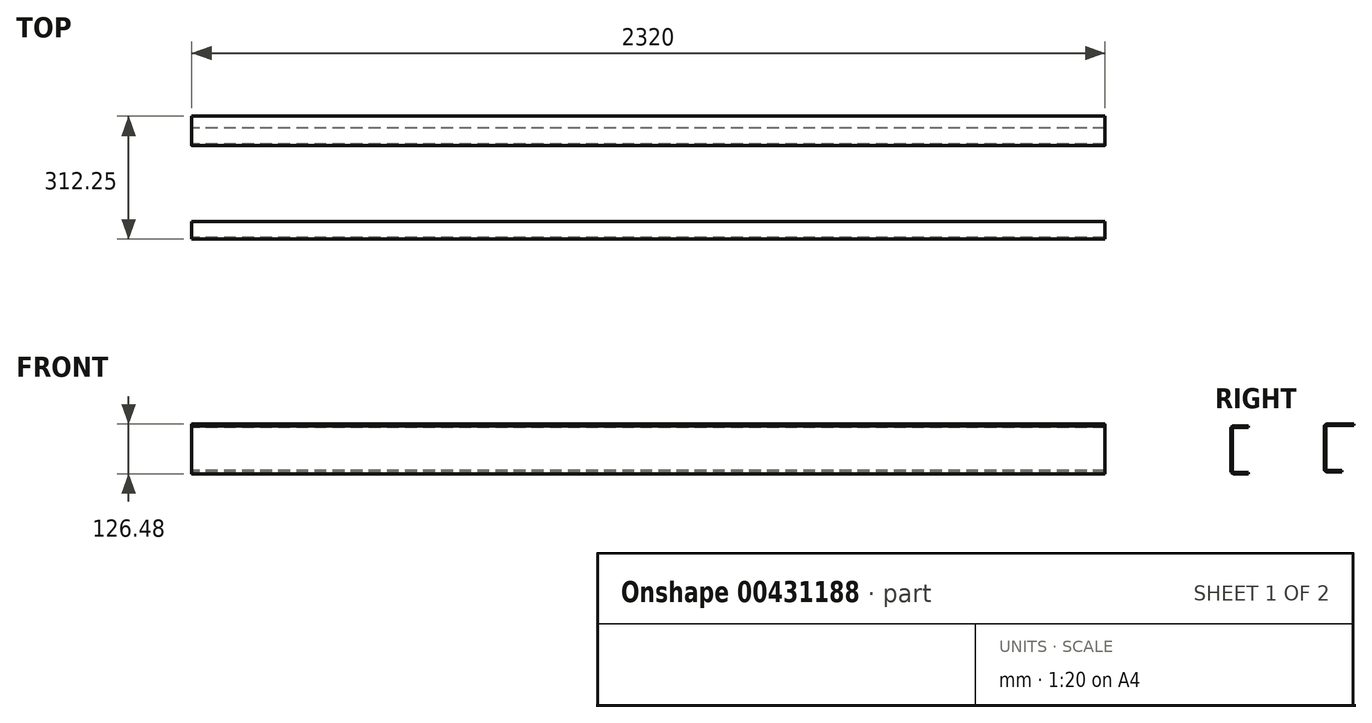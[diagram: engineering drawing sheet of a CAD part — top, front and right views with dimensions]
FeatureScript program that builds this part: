
annotation { "Feature Type Name" : "Feature", "Feature Type Description" : "" }
export const myFeature = defineFeature(function(context is Context, id is Id, definition is map)
    precondition{}
    {
        {
            var Q0;
            Q0=qCreatedBy(makeId("Right.planeOp"),FACE);
            var sketch = newSketch(context, id + "F0", { "sketchPlane" : qUnion([Q0])});
            skLineSegment(sketch, "E0", {"start": v(0, 8) * mm, "end": v(0, 114) * mm});
            skLineSegment(sketch, "E1", {"start": v(8, 122) * mm, "end": v(45, 122) * mm});
            skLineSegment(sketch, "E2", {"start": v(8, 0) * mm, "end": v(45, 0) * mm});
            skLineSegment(sketch, "E3.0", {"start": v(8, 118) * mm, "end": v(45, 118) * mm});
            skLineSegment(sketch, "E4.0", {"start": v(4, 8) * mm, "end": v(4, 114) * mm});
            skLineSegment(sketch, "E5.0", {"start": v(8, 4) * mm, "end": v(45, 4) * mm});
            skLineSegment(sketch, "E6", {"start": v(45, 118) * mm, "end": v(45, 122) * mm});
            skLineSegment(sketch, "E7", {"start": v(45, 0) * mm, "end": v(45, 4) * mm});
            skPoint(sketch, "E8.visualSharp", {"position": v(0, 122) * mm});
            skPoint(sketch, "E9.visualSharp", {"position": v(4, 118) * mm});
            skArc(sketch, "E9.filletArc", {"start": v(8, 118) * mm, "mid": v(5.17, 116.83) * mm, "end": v(4, 114) * mm});
            skArc(sketch, "E10.0", {"start": v(8, 122) * mm, "mid": v(2.34, 119.66) * mm, "end": v(0, 114) * mm});
            skPoint(sketch, "E11.visualSharp", {"position": v(4, 4) * mm});
            skArc(sketch, "E11.filletArc", {"start": v(4, 8) * mm, "mid": v(5.17, 5.17) * mm, "end": v(8, 4) * mm});
            skArc(sketch, "E12.0", {"start": v(0, 8) * mm, "mid": v(2.34, 2.34) * mm, "end": v(8, 0) * mm});
            skPoint(sketch, "E13.orphan", {"position": v(0, 0) * mm});
            skSolve(sketch);
        }
        {
            var Q0;
            Q0=makeQuery(id+"F0.imprint","IMPRINT",FACE,{"disambiguationData":[TD([[makeQuery(id+"F0.imprint","IMPRINT",EDGE,{"derivedFrom":sQuery(id+"F0.wireOp",EDGE,"E0")}),-1.0]])]});
            extrude(context, id + "F1", {"entities" : qUnion([Q0]), "depth" : 2320 * mm});
        }
        {
            var Q0;
            Q0=qCreatedBy(makeId("Right.planeOp"),FACE);
            var sketch = newSketch(context, id + "F2", { "sketchPlane" : qUnion([Q0])});
            skLineSegment(sketch, "E14", {"start": v(237.25, 12.48) * mm, "end": v(237.25, 118.48) * mm});
            skLineSegment(sketch, "E15", {"start": v(245.25, 126.48) * mm, "end": v(312.25, 126.48) * mm});
            skLineSegment(sketch, "E16", {"start": v(245.25, 4.48) * mm, "end": v(282.25, 4.48) * mm});
            skLineSegment(sketch, "E17.0", {"start": v(245.25, 122.48) * mm, "end": v(312.25, 122.48) * mm});
            skLineSegment(sketch, "E18.0", {"start": v(241.25, 12.48) * mm, "end": v(241.25, 118.48) * mm});
            skLineSegment(sketch, "E19.0", {"start": v(245.25, 8.48) * mm, "end": v(282.25, 8.48) * mm});
            skLineSegment(sketch, "E20", {"start": v(312.25, 122.48) * mm, "end": v(312.25, 126.48) * mm});
            skLineSegment(sketch, "E21", {"start": v(282.25, 4.48) * mm, "end": v(282.25, 8.48) * mm});
            skPoint(sketch, "E22.visualSharp", {"position": v(237.25, 126.48) * mm});
            skPoint(sketch, "E23.visualSharp", {"position": v(241.25, 122.48) * mm});
            skArc(sketch, "E23.filletArc", {"start": v(245.25, 122.48) * mm, "mid": v(242.42, 121.3) * mm, "end": v(241.25, 118.48) * mm});
            skArc(sketch, "E24.0", {"start": v(245.25, 126.48) * mm, "mid": v(239.6, 124.14) * mm, "end": v(237.25, 118.48) * mm});
            skPoint(sketch, "E25.visualSharp", {"position": v(241.25, 8.48) * mm});
            skArc(sketch, "E25.filletArc", {"start": v(241.25, 12.48) * mm, "mid": v(242.42, 9.65) * mm, "end": v(245.25, 8.48) * mm});
            skArc(sketch, "E26.0", {"start": v(237.25, 12.48) * mm, "mid": v(239.6, 6.82) * mm, "end": v(245.25, 4.48) * mm});
            skPoint(sketch, "E27.orphan", {"position": v(237.25, 4.48) * mm});
            skSolve(sketch);
        }
        {
            var Q0;
            Q0=makeQuery(id+"F2.imprint","IMPRINT",FACE,{"disambiguationData":[TD([[makeQuery(id+"F2.imprint","IMPRINT",EDGE,{"derivedFrom":sQuery(id+"F2.wireOp",EDGE,"E14")}),-1.0]])]});
            extrude(context, id + "F3", {"entities" : qUnion([Q0]), "depth" : 2320 * mm});
        }
    });
